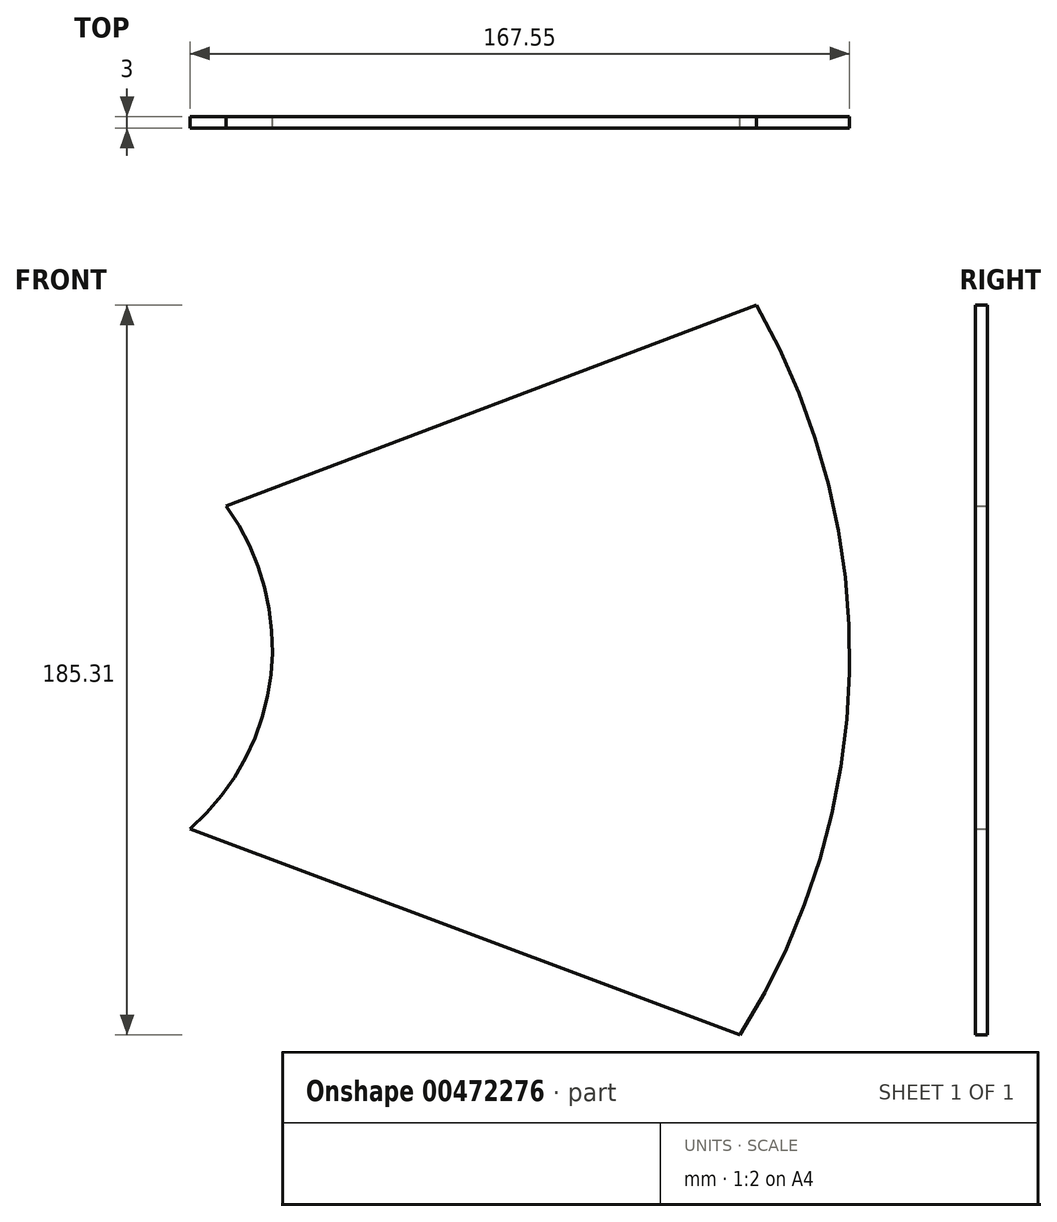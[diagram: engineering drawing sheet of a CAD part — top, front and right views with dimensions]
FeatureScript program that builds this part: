
annotation { "Feature Type Name" : "Feature", "Feature Type Description" : "" }
export const myFeature = defineFeature(function(context is Context, id is Id, definition is map)
    precondition{}
    {
        {
            var Q0;
            Q0=qCreatedBy(makeId("Front.planeOp"),FACE);
            var sketch = newSketch(context, id + "F0", { "sketchPlane" : qUnion([Q0])});
            skLineSegment(sketch, "E0", {"start": v(21.62, 148.16) * mm, "end": v(161.15, 201) * mm});
            skLineSegment(sketch, "E1", {"start": v(12.45, 66.18) * mm, "end": v(152.19, 13.88) * mm});
            skArc(sketch, "E2.trimOffspring", {"start": v(12.45, 66.18) * mm, "mid": v(32.98, 105.38) * mm, "end": v(21.62, 148.16) * mm});
            skPoint(sketch, "E3.end.orphan", {"position": v(41.5, 0) * mm});
            skPoint(sketch, "E4.top.end.orphan", {"position": v(220, 220) * mm});
            skArc(sketch, "E5", {"start": v(152.19, 13.88) * mm, "mid": v(179.95, 105.96) * mm, "end": v(156.35, 199.19) * mm});
            skPoint(sketch, "E6.center.orphan", {"position": v(220, 110) * mm});
            skPoint(sketch, "E7.orphan", {"position": v(220, 0) * mm});
            skPoint(sketch, "E8.orphan", {"position": v(0, 220) * mm});
            skPoint(sketch, "E4.bottom.start.orphan", {"position": v(0, 0) * mm});
            skSolve(sketch);
        }
        {
            var Q0;
            Q0=makeQuery(id+"F0.imprint","IMPRINT",FACE,{"disambiguationData":[TD([[makeQuery(id+"F0.imprint","IMPRINT",EDGE,{"derivedFrom":sQuery(id+"F0.wireOp",EDGE,"E1")}),1.0]])]});
            extrude(context, id + "F1", {"entities" : qUnion([Q0]), "depth" : 3 * mm});
        }
    });
